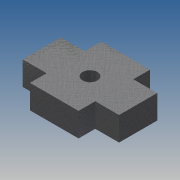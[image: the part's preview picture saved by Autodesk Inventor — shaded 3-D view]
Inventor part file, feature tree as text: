
AUTODESK INVENTOR PART (.ipt)
format: ipt  version: 2015 SP1 (Build 190203100, 203)  size: 116,736 bytes
history: native  units: mm
features: extrude x1, sketch x1
ambient origin geometry x8: Origin, YZ Plane, XZ Plane, XY Plane, X Axis, Y Axis, Z Axis, Center Point
bodies: Volumenkörper1 (feature_tree)
feature tree (2):
  extrude  "Extrusion1"  Depth=15.0mm
  sketch  "Skizze1"  dims[d0=10.2mm d1=15.0mm d2=5.0mm d3=8.0mm d4=3.1mm d5=5.0mm d6=0.0mm]
